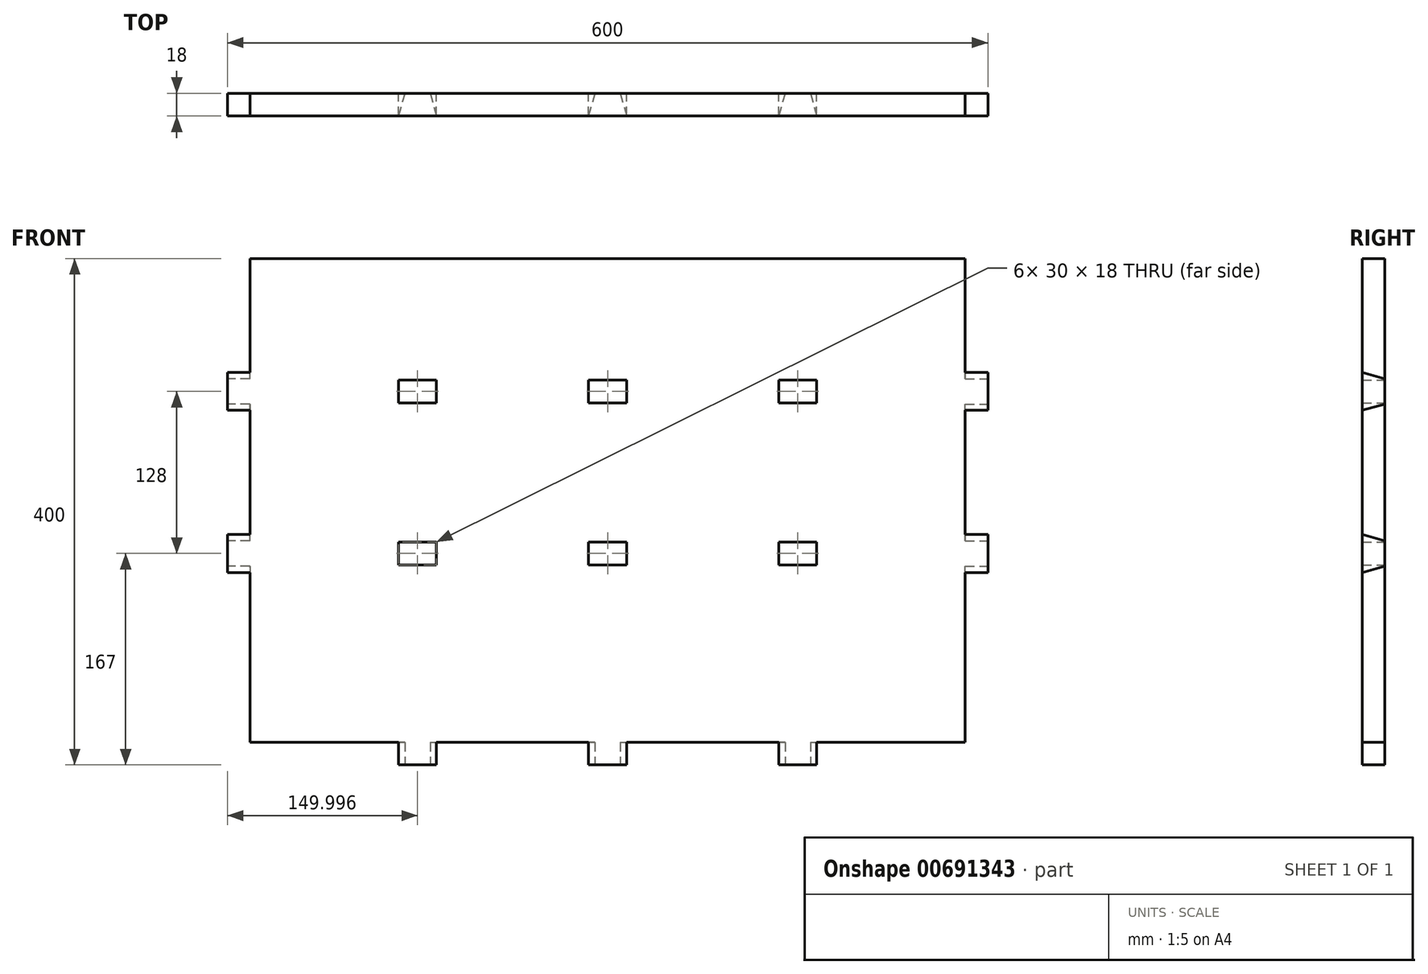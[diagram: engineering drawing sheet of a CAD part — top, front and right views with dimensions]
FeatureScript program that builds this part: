
annotation { "Feature Type Name" : "Feature", "Feature Type Description" : "" }
export const myFeature = defineFeature(function(context is Context, id is Id, definition is map)
    precondition{}
    {
        {
            var Q0;
            Q0=qCreatedBy(makeId("Top.planeOp"),FACE);
            var sketch = newSketch(context, id + "F0", { "sketchPlane" : qUnion([Q0])});
            skLineSegment(sketch, "E0", {"start": v(-0.06, -318.27) * mm, "end": v(-0.06, 208.58) * mm, "construction": true});
            skLineSegment(sketch, "E1", {"start": v(-352.66, -70.99) * mm, "end": v(361, -70.99) * mm, "construction": true});
            skLineSegment(sketch, "E2", {"start": v(-10.06, 129.01) * mm, "end": v(-15.06, 111.01) * mm});
            skLineSegment(sketch, "E3", {"start": v(-15.06, 111.01) * mm, "end": v(-0.06, 111.01) * mm});
            skLineSegment(sketch, "E4", {"start": v(-10.06, 129.01) * mm, "end": v(-0.06, 129.01) * mm});
            skLineSegment(sketch, "E5.MirrorCS", {"start": v(9.94, 129.01) * mm, "end": v(14.94, 111.01) * mm});
            skLineSegment(sketch, "E6", {"start": v(-0.06, 111.01) * mm, "end": v(14.94, 111.01) * mm});
            skLineSegment(sketch, "E7", {"start": v(-0.06, 129.01) * mm, "end": v(9.94, 129.01) * mm});
            skLineSegment(sketch, "E8.1.0.0", {"start": v(139.94, 129.01) * mm, "end": v(134.94, 111.01) * mm});
            skLineSegment(sketch, "E8.1.0.1", {"start": v(139.94, 129.01) * mm, "end": v(149.94, 129.01) * mm});
            skLineSegment(sketch, "E8.1.0.2", {"start": v(149.94, 129.01) * mm, "end": v(159.94, 129.01) * mm});
            skLineSegment(sketch, "E8.1.0.3", {"start": v(159.94, 129.01) * mm, "end": v(164.94, 111.01) * mm});
            skLineSegment(sketch, "E9.1.0.0", {"start": v(-160.06, 129.01) * mm, "end": v(-165.06, 111.01) * mm});
            skLineSegment(sketch, "E9.1.0.1", {"start": v(-160.06, 129.01) * mm, "end": v(-150.06, 129.01) * mm});
            skLineSegment(sketch, "E9.1.0.2", {"start": v(-150.06, 129.01) * mm, "end": v(-140.06, 129.01) * mm});
            skLineSegment(sketch, "E9.1.0.3", {"start": v(-140.06, 129.01) * mm, "end": v(-135.06, 111.01) * mm});
            skLineSegment(sketch, "E10", {"start": v(164.94, 111.01) * mm, "end": v(134.94, 111.01) * mm});
            skLineSegment(sketch, "E11", {"start": v(-135.06, 111.01) * mm, "end": v(-165.06, 111.01) * mm});
            skLineSegment(sketch, "E12", {"start": v(-300.06, -10.99) * mm, "end": v(-300.06, -0.99) * mm, "construction": true});
            skLineSegment(sketch, "E13", {"start": v(-300.06, -0.99) * mm, "end": v(-282.06, -0.99) * mm, "construction": true});
            skLineSegment(sketch, "E14", {"start": v(-300.06, -0.99) * mm, "end": v(-300.06, 9.01) * mm});
            skLineSegment(sketch, "E15", {"start": v(-300.06, 9.01) * mm, "end": v(-282.06, 14.01) * mm});
            skLineSegment(sketch, "E16", {"start": v(-282.06, 14.01) * mm, "end": v(-282.06, -0.99) * mm});
            skLineSegment(sketch, "E17.MirrorCS", {"start": v(-300.06, -0.99) * mm, "end": v(-300.06, -10.99) * mm});
            skLineSegment(sketch, "E18.MirrorCS", {"start": v(-300.06, -10.99) * mm, "end": v(-282.06, -15.99) * mm});
            skLineSegment(sketch, "E19.MirrorCS", {"start": v(-282.06, -15.99) * mm, "end": v(-282.06, -0.99) * mm});
            skLineSegment(sketch, "E20.MirrorCS", {"start": v(-300.06, -130.99) * mm, "end": v(-282.06, -125.99) * mm});
            skLineSegment(sketch, "E21.MirrorCS", {"start": v(-282.06, -125.99) * mm, "end": v(-282.06, -140.99) * mm});
            skLineSegment(sketch, "E22.MirrorCS", {"start": v(-282.06, -155.99) * mm, "end": v(-282.06, -140.99) * mm});
            skLineSegment(sketch, "E23.MirrorCS", {"start": v(-300.06, -150.99) * mm, "end": v(-282.06, -155.99) * mm});
            skLineSegment(sketch, "E24.MirrorCS", {"start": v(-300.06, -140.99) * mm, "end": v(-300.06, -150.99) * mm});
            skLineSegment(sketch, "E25.MirrorCS", {"start": v(299.94, 9.01) * mm, "end": v(281.94, 14.01) * mm});
            skLineSegment(sketch, "E26.MirrorCS", {"start": v(281.94, 14.01) * mm, "end": v(281.94, -0.99) * mm});
            skLineSegment(sketch, "E27.MirrorCS", {"start": v(299.94, -0.99) * mm, "end": v(299.94, 9.01) * mm});
            skLineSegment(sketch, "E28.MirrorCS", {"start": v(299.94, -10.99) * mm, "end": v(281.94, -15.99) * mm});
            skLineSegment(sketch, "E29.MirrorCS", {"start": v(281.94, -15.99) * mm, "end": v(281.94, -0.99) * mm});
            skLineSegment(sketch, "E30.MirrorCS", {"start": v(299.94, -0.99) * mm, "end": v(299.94, -10.99) * mm});
            skLineSegment(sketch, "E31.MirrorCS", {"start": v(299.94, -0.99) * mm, "end": v(281.94, -0.99) * mm, "construction": true});
            skLineSegment(sketch, "E32.MirrorCS", {"start": v(299.94, -150.99) * mm, "end": v(281.94, -155.99) * mm});
            skLineSegment(sketch, "E33.MirrorCS", {"start": v(281.94, -125.99) * mm, "end": v(281.94, -140.99) * mm});
            skLineSegment(sketch, "E34.MirrorCS", {"start": v(281.94, -155.99) * mm, "end": v(281.94, -140.99) * mm});
            skLineSegment(sketch, "E35.MirrorCS", {"start": v(299.94, -130.99) * mm, "end": v(281.94, -125.99) * mm});
            skLineSegment(sketch, "E36.MirrorCS", {"start": v(299.94, -140.99) * mm, "end": v(299.94, -150.99) * mm});
            skLineSegment(sketch, "E37.MirrorCS", {"start": v(299.94, -10.99) * mm, "end": v(299.94, -0.99) * mm, "construction": true});
            skLineSegment(sketch, "E38", {"start": v(-300.06, -140.99) * mm, "end": v(-300.06, -130.99) * mm});
            skLineSegment(sketch, "E39", {"start": v(299.94, -140.99) * mm, "end": v(299.94, -130.99) * mm});
            skPoint(sketch, "E40.orphan", {"position": v(299.94, -70.99) * mm});
            skPoint(sketch, "E41.orphan", {"position": v(-300.06, -70.99) * mm});
            skSolve(sketch);
        }
        {
            var Q0;
            Q0=qCreatedBy(makeId("Front.planeOp"),FACE);
            var Q1;
            Q1=sQuery(id+"F0.wireOp",VERTEX,"E2.start");
            cPlane(context, id + "F1", {"entities" : qUnion([Q0, Q1]), "cplaneType" : CPlaneType.PLANE_POINT, "offset" : 150 * mm, "oppositeDirection" : true, "width" : 150 * mm, "height" : 150 * mm});
        }
        {
            var Q0;
            Q0=qCreatedBy(makeId("Right.planeOp"),FACE);
            var Q1;
            Q1=sQuery(id+"F0.wireOp",VERTEX,"E28.MirrorCS.start");
            cPlane(context, id + "F2", {"entities" : qUnion([Q0, Q1]), "cplaneType" : CPlaneType.PLANE_POINT, "offset" : 25 * mm, "width" : 150 * mm, "height" : 150 * mm});
        }
        {
            var Q0;
            Q0=qCreatedBy(id+"F2.planeOp",FACE);
            var sketch = newSketch(context, id + "F3", { "sketchPlane" : qUnion([Q0])});
            skPoint(sketch, "E42.0", {"position": v(-150.99, 0) * mm});
            skLineSegment(sketch, "E43.0", {"start": v(-150.99, 18) * mm, "end": v(-150.99, 0) * mm});
            skLineSegment(sketch, "E44.0", {"start": v(-150.99, 18) * mm, "end": v(-130.99, 18) * mm});
            skLineSegment(sketch, "E45.0", {"start": v(-130.99, 18) * mm, "end": v(-130.99, 0) * mm});
            skLineSegment(sketch, "E46.0", {"start": v(-150.99, 0) * mm, "end": v(-130.99, 0) * mm});
            skLineSegment(sketch, "E47.0.0", {"start": v(-10.99, 0) * mm, "end": v(9.01, 0) * mm});
            skLineSegment(sketch, "E47.0.1", {"start": v(9.01, 0) * mm, "end": v(9.01, 18) * mm});
            skLineSegment(sketch, "E47.0.2", {"start": v(9.01, 18) * mm, "end": v(-10.99, 18) * mm});
            skLineSegment(sketch, "E47.0.3", {"start": v(-10.99, 18) * mm, "end": v(-10.99, 0) * mm});
            skLineSegment(sketch, "E48.0", {"start": v(-270.99, 0) * mm, "end": v(-150.99, 0) * mm});
            skLineSegment(sketch, "E49.0", {"start": v(-70.99, 0) * mm, "end": v(-130.99, 0) * mm});
            skLineSegment(sketch, "E50.0", {"start": v(-70.99, 0) * mm, "end": v(-10.99, 0) * mm});
            skLineSegment(sketch, "E51.0", {"start": v(129.01, 0) * mm, "end": v(9.01, 0) * mm});
            skLineSegment(sketch, "E52", {"start": v(-130.99, 18) * mm, "end": v(-10.99, 18) * mm});
            skLineSegment(sketch, "E53", {"start": v(-150.99, 18) * mm, "end": v(-270.99, 18) * mm});
            skLineSegment(sketch, "E54", {"start": v(9.01, 18) * mm, "end": v(129.01, 18) * mm});
            skLineSegment(sketch, "E55", {"start": v(-270.99, 18) * mm, "end": v(-270.99, 0) * mm});
            skLineSegment(sketch, "E56", {"start": v(129.01, 18) * mm, "end": v(129.01, 0) * mm});
            skLineSegment(sketch, "E57.bottom", {"start": v(129.01, 18) * mm, "end": v(-270.99, 18) * mm});
            skLineSegment(sketch, "E57.top", {"start": v(129.01, 400) * mm, "end": v(-270.99, 400) * mm});
            skLineSegment(sketch, "E57.left", {"start": v(129.01, 18) * mm, "end": v(129.01, 400) * mm});
            skLineSegment(sketch, "E57.right", {"start": v(-270.99, 18) * mm, "end": v(-270.99, 400) * mm});
            skLineSegment(sketch, "E58", {"start": v(-140.99, 18) * mm, "end": v(-140.99, 313.42) * mm, "construction": true});
            skLineSegment(sketch, "E59", {"start": v(-0.99, 18) * mm, "end": v(-0.99, 349.98) * mm, "construction": true});
            skLineSegment(sketch, "E60", {"start": v(-312.14, 158) * mm, "end": v(190.47, 158) * mm, "construction": true});
            skLineSegment(sketch, "E61", {"start": v(-304.14, 286) * mm, "end": v(174.47, 286) * mm, "construction": true});
            skLineSegment(sketch, "E62", {"start": v(-312.14, 176) * mm, "end": v(194.1, 176) * mm, "construction": true});
            skLineSegment(sketch, "E63", {"start": v(-306.06, 304) * mm, "end": v(175.74, 304) * mm, "construction": true});
            skLineSegment(sketch, "E64", {"start": v(173.45, 391) * mm, "end": v(-324.33, 391) * mm, "construction": true});
            skLineSegment(sketch, "E65.bottom", {"start": v(-140.99, 176) * mm, "end": v(-125.99, 176) * mm});
            skLineSegment(sketch, "E65.top", {"start": v(-140.99, 158) * mm, "end": v(-125.99, 158) * mm});
            skLineSegment(sketch, "E65.left", {"start": v(-140.99, 176) * mm, "end": v(-140.99, 158) * mm});
            skLineSegment(sketch, "E65.right", {"start": v(-125.99, 176) * mm, "end": v(-125.99, 158) * mm});
            skLineSegment(sketch, "E66.MirrorCS", {"start": v(-155.99, 176) * mm, "end": v(-155.99, 158) * mm});
            skLineSegment(sketch, "E67", {"start": v(-140.99, 158) * mm, "end": v(-155.99, 158) * mm});
            skLineSegment(sketch, "E68", {"start": v(-155.99, 176) * mm, "end": v(-140.99, 176) * mm});
            skLineSegment(sketch, "E69.1.0.0", {"start": v(14.01, 176) * mm, "end": v(14.01, 158) * mm});
            skLineSegment(sketch, "E69.1.0.1", {"start": v(-15.99, 176) * mm, "end": v(-15.99, 158) * mm});
            skLineSegment(sketch, "E69.direction1", {"start": v(-125.99, 158) * mm, "end": v(14.01, 158) * mm, "construction": true});
            skLineSegment(sketch, "E70", {"start": v(-15.99, 176) * mm, "end": v(14.01, 176) * mm});
            skLineSegment(sketch, "E71", {"start": v(-15.99, 158) * mm, "end": v(14.01, 158) * mm});
            skLineSegment(sketch, "E72", {"start": v(-155.99, 176) * mm, "end": v(-155.99, 421.76) * mm, "construction": true});
            skLineSegment(sketch, "E73", {"start": v(-125.99, 176) * mm, "end": v(-125.99, 428.96) * mm, "construction": true});
            skLineSegment(sketch, "E74", {"start": v(-15.99, 176) * mm, "end": v(-15.99, 432.16) * mm, "construction": true});
            skLineSegment(sketch, "E75", {"start": v(14.01, 176) * mm, "end": v(14.01, 435.36) * mm, "construction": true});
            skLineSegment(sketch, "E76.bottom", {"start": v(-155.99, 304) * mm, "end": v(-125.99, 304) * mm});
            skLineSegment(sketch, "E76.top", {"start": v(-155.99, 286) * mm, "end": v(-125.99, 286) * mm});
            skLineSegment(sketch, "E76.left", {"start": v(-155.99, 304) * mm, "end": v(-155.99, 286) * mm});
            skLineSegment(sketch, "E76.right", {"start": v(-125.99, 304) * mm, "end": v(-125.99, 286) * mm});
            skLineSegment(sketch, "E77.bottom", {"start": v(14.01, 286) * mm, "end": v(-15.99, 286) * mm});
            skLineSegment(sketch, "E77.top", {"start": v(14.01, 304) * mm, "end": v(-15.99, 304) * mm});
            skLineSegment(sketch, "E77.left", {"start": v(14.01, 286) * mm, "end": v(14.01, 304) * mm});
            skLineSegment(sketch, "E77.right", {"start": v(-15.99, 286) * mm, "end": v(-15.99, 304) * mm});
            skLineSegment(sketch, "E78", {"start": v(111.01, 481.52) * mm, "end": v(111.01, -48.3) * mm, "construction": true});
            skLineSegment(sketch, "E79", {"start": v(14.01, 167) * mm, "end": v(206.7, 167) * mm, "construction": true});
            skLineSegment(sketch, "E80", {"start": v(14.01, 295) * mm, "end": v(175.74, 295) * mm, "construction": true});
            skLineSegment(sketch, "E81", {"start": v(111.01, 295) * mm, "end": v(111.01, 310) * mm});
            skLineSegment(sketch, "E82", {"start": v(111.01, 310) * mm, "end": v(129.01, 305) * mm});
            skLineSegment(sketch, "E83", {"start": v(129.01, 305) * mm, "end": v(129.01, 295) * mm});
            skLineSegment(sketch, "E84.MirrorCS", {"start": v(111.01, 280) * mm, "end": v(129.01, 285) * mm});
            skLineSegment(sketch, "E85", {"start": v(111.01, 295) * mm, "end": v(111.01, 280) * mm});
            skLineSegment(sketch, "E86", {"start": v(129.01, 285) * mm, "end": v(129.01, 295) * mm, "construction": true});
            skLineSegment(sketch, "E87.0.1.0", {"start": v(111.01, 152) * mm, "end": v(129.01, 157) * mm});
            skLineSegment(sketch, "E87.0.1.1", {"start": v(111.01, 182) * mm, "end": v(129.01, 177) * mm});
            skLineSegment(sketch, "E87.direction1", {"start": v(111.01, 280) * mm, "end": v(136.01, 280) * mm, "construction": true});
            skLineSegment(sketch, "E87.direction2", {"start": v(111.01, 280) * mm, "end": v(111.01, 152) * mm, "construction": true});
            skLineSegment(sketch, "E88", {"start": v(111.01, 182) * mm, "end": v(111.01, 152) * mm});
            skLineSegment(sketch, "E89", {"start": v(129.01, 157) * mm, "end": v(129.01, 177) * mm});
            skLineSegment(sketch, "E90", {"start": v(129.01, 305) * mm, "end": v(129.01, 285) * mm});
            skLineSegment(sketch, "E91", {"start": v(111.01, 280) * mm, "end": v(111.01, 310) * mm});
            skSolve(sketch);
        }
        {
            var Q0;
            Q0=qCreatedBy(id+"F1.planeOp",FACE);
            var sketch = newSketch(context, id + "F4", { "sketchPlane" : qUnion([Q0])});
            skLineSegment(sketch, "E92.bottom", {"start": v(-300.2, 0) * mm, "end": v(299.94, 0) * mm});
            skLineSegment(sketch, "E92.top", {"start": v(-300.2, 400) * mm, "end": v(299.94, 400) * mm});
            skLineSegment(sketch, "E92.left", {"start": v(-300.2, 0) * mm, "end": v(-300.2, 400) * mm});
            skLineSegment(sketch, "E92.right", {"start": v(299.94, 0) * mm, "end": v(299.94, 400) * mm});
            skLineSegment(sketch, "E93.0", {"start": v(281.94, 0) * mm, "end": v(281.94, 400) * mm});
            skLineSegment(sketch, "E94.0", {"start": v(-282.2, 0) * mm, "end": v(-282.2, 400) * mm});
            skLineSegment(sketch, "E95.0", {"start": v(-300.2, 18) * mm, "end": v(299.94, 18) * mm});
            skSolve(sketch);
        }
        {
            var Q0;
            {var subQ0=sQuery(id+"F4.wireOp",EDGE,"E93.0");var subQ1=sQuery(id+"F4.wireOp",EDGE,"E92.top");var subQ2=makeQuery(id+"F4.imprint","INTERSECT",VERTEX,{"derivedFrom":[subQ1,subQ0]});Q0=makeQuery(id+"F4.imprint","IMPRINT",FACE,{"disambiguationData":[TD([[makeQuery(id+"F4.imprint","IMPRINT",EDGE,{"disambiguationData":[TD([[subQ2,1.0]])],"derivedFrom":subQ1}),-1.0]])]});}
            extrude(context, id + "F5", {"entities" : qUnion([Q0]), "depth" : 18 * mm, "offsetDistance" : 25 * mm});
        }
        {
            var Q0;
            Q0=makeQuery(id+"F0.imprint","IMPRINT",FACE,{"disambiguationData":[TD([[makeQuery(id+"F0.imprint","IMPRINT",EDGE,{"derivedFrom":sQuery(id+"F0.wireOp",EDGE,"E8.1.0.0")}),1.0]])]});
            var Q1;
            Q1=makeQuery(id+"F0.imprint","IMPRINT",FACE,{"disambiguationData":[TD([[makeQuery(id+"F0.imprint","IMPRINT",EDGE,{"derivedFrom":sQuery(id+"F0.wireOp",EDGE,"E2")}),1.0]])]});
            var Q2;
            Q2=makeQuery(id+"F0.imprint","IMPRINT",FACE,{"disambiguationData":[TD([[makeQuery(id+"F0.imprint","IMPRINT",EDGE,{"derivedFrom":sQuery(id+"F0.wireOp",EDGE,"E9.1.0.0")}),1.0]])]});
            var Q3;
            Q3=makeQuery(id+"F5.opExtrude","SWEPT_FACE",FACE,{"disambiguationData":[OSD([sQuery(id+"F4.wireOp",EDGE,"E95.0")])]});
            extrude(context, id + "F6", {"entities" : qUnion([Q0, Q1, Q2]), "operationType" : NewBodyOperationType.ADD, "endBound" : BoundingType.UP_TO_SURFACE, "depth" : 18 * mm, "endBoundEntityFace" : qUnion([Q3]), "offsetDistance" : 25 * mm});
        }
        {
            var Q0;
            Q0=makeQuery(id+"F3.imprint","IMPRINT",FACE,{"disambiguationData":[TD([[makeQuery(id+"F3.imprint","IMPRINT",EDGE,{"derivedFrom":sQuery(id+"F3.wireOp",EDGE,"E87.0.1.0")}),1.0]])]});
            var Q1;
            {var subQ0=sQuery(id+"F3.wireOp",EDGE,"E82");Q1=makeQuery(id+"F3.imprint","IMPRINT",FACE,{"disambiguationData":[TD([[makeQuery(id+"F3.imprint","IMPRINT",EDGE,{"derivedFrom":subQ0}),-1.0]])]});}
            var Q2;
            Q2=makeQuery(id+"F5.opExtrude","SWEPT_FACE",FACE,{"disambiguationData":[OSD([sQuery(id+"F4.wireOp",EDGE,"E93.0")])]});
            extrude(context, id + "F7", {"entities" : qUnion([Q0, Q1]), "operationType" : NewBodyOperationType.ADD, "endBound" : BoundingType.UP_TO_SURFACE, "oppositeDirection" : true, "depth" : 25 * mm, "endBoundEntityFace" : qUnion([Q2]), "offsetDistance" : 25 * mm});
        }
        {
            var Q0;
            Q0=qCreatedBy(id+"F2.planeOp",FACE);
            cPlane(context, id + "F8", {"entities" : qUnion([Q0]), "cplaneType" : CPlaneType.OFFSET, "offset" : 600 * mm, "oppositeDirection" : true, "width" : 150 * mm, "height" : 150 * mm});
        }
        {
            var Q0;
            Q0=qCreatedBy(id+"F8.planeOp",FACE);
            var sketch = newSketch(context, id + "F9", { "sketchPlane" : qUnion([Q0])});
            skPoint(sketch, "E96.0", {"position": v(-150.99, 0) * mm});
            skLineSegment(sketch, "E97.0", {"start": v(-150.99, 18) * mm, "end": v(-150.99, 0) * mm});
            skLineSegment(sketch, "E98.0", {"start": v(-150.99, 18) * mm, "end": v(-130.99, 18) * mm});
            skLineSegment(sketch, "E99.0", {"start": v(-130.99, 18) * mm, "end": v(-130.99, 0) * mm});
            skLineSegment(sketch, "E100.0", {"start": v(-150.99, 0) * mm, "end": v(-130.99, 0) * mm});
            skLineSegment(sketch, "E101.0.0", {"start": v(-10.99, 0) * mm, "end": v(9.01, 0) * mm});
            skLineSegment(sketch, "E101.0.1", {"start": v(9.01, 0) * mm, "end": v(9.01, 18) * mm});
            skLineSegment(sketch, "E101.0.2", {"start": v(9.01, 18) * mm, "end": v(-10.99, 18) * mm});
            skLineSegment(sketch, "E101.0.3", {"start": v(-10.99, 18) * mm, "end": v(-10.99, 0) * mm});
            skLineSegment(sketch, "E102.0", {"start": v(-270.99, 0) * mm, "end": v(-150.99, 0) * mm});
            skLineSegment(sketch, "E103.0", {"start": v(-70.99, 0) * mm, "end": v(-130.99, 0) * mm});
            skLineSegment(sketch, "E104.0", {"start": v(-70.99, 0) * mm, "end": v(-10.99, 0) * mm});
            skLineSegment(sketch, "E105.0", {"start": v(129.01, 0) * mm, "end": v(9.01, 0) * mm});
            skLineSegment(sketch, "E106", {"start": v(-130.99, 18) * mm, "end": v(-10.99, 18) * mm});
            skLineSegment(sketch, "E107", {"start": v(-150.99, 18) * mm, "end": v(-270.99, 18) * mm});
            skLineSegment(sketch, "E108", {"start": v(9.01, 18) * mm, "end": v(129.01, 18) * mm});
            skLineSegment(sketch, "E109", {"start": v(-270.99, 18) * mm, "end": v(-270.99, 0) * mm});
            skLineSegment(sketch, "E110", {"start": v(129.01, 18) * mm, "end": v(129.01, 0) * mm});
            skLineSegment(sketch, "E111.bottom", {"start": v(129.01, 18) * mm, "end": v(-270.99, 18) * mm});
            skLineSegment(sketch, "E111.top", {"start": v(129.01, 400) * mm, "end": v(-270.99, 400) * mm});
            skLineSegment(sketch, "E111.left", {"start": v(129.01, 18) * mm, "end": v(129.01, 400) * mm});
            skLineSegment(sketch, "E111.right", {"start": v(-270.99, 18) * mm, "end": v(-270.99, 400) * mm});
            skLineSegment(sketch, "E112", {"start": v(-140.99, 18) * mm, "end": v(-140.99, 313.42) * mm, "construction": true});
            skLineSegment(sketch, "E113", {"start": v(-0.99, 18) * mm, "end": v(-0.99, 349.98) * mm, "construction": true});
            skLineSegment(sketch, "E114", {"start": v(-312.14, 158) * mm, "end": v(190.47, 158) * mm, "construction": true});
            skLineSegment(sketch, "E115", {"start": v(-304.14, 286) * mm, "end": v(174.47, 286) * mm, "construction": true});
            skLineSegment(sketch, "E116", {"start": v(-312.14, 176) * mm, "end": v(194.1, 176) * mm, "construction": true});
            skLineSegment(sketch, "E117", {"start": v(-306.06, 304) * mm, "end": v(175.74, 304) * mm, "construction": true});
            skLineSegment(sketch, "E118", {"start": v(173.45, 391) * mm, "end": v(-324.33, 391) * mm, "construction": true});
            skLineSegment(sketch, "E119.bottom", {"start": v(-140.99, 176) * mm, "end": v(-125.99, 176) * mm});
            skLineSegment(sketch, "E119.top", {"start": v(-140.99, 158) * mm, "end": v(-125.99, 158) * mm});
            skLineSegment(sketch, "E119.left", {"start": v(-140.99, 176) * mm, "end": v(-140.99, 158) * mm});
            skLineSegment(sketch, "E119.right", {"start": v(-125.99, 176) * mm, "end": v(-125.99, 158) * mm});
            skLineSegment(sketch, "E120.MirrorCS", {"start": v(-155.99, 176) * mm, "end": v(-155.99, 158) * mm});
            skLineSegment(sketch, "E121", {"start": v(-140.99, 158) * mm, "end": v(-155.99, 158) * mm});
            skLineSegment(sketch, "E122", {"start": v(-155.99, 176) * mm, "end": v(-140.99, 176) * mm});
            skLineSegment(sketch, "E123.1.0.0", {"start": v(14.01, 176) * mm, "end": v(14.01, 158) * mm});
            skLineSegment(sketch, "E123.1.0.1", {"start": v(-15.99, 176) * mm, "end": v(-15.99, 158) * mm});
            skLineSegment(sketch, "E123.direction1", {"start": v(-125.99, 158) * mm, "end": v(14.01, 158) * mm, "construction": true});
            skLineSegment(sketch, "E124", {"start": v(-15.99, 176) * mm, "end": v(14.01, 176) * mm});
            skLineSegment(sketch, "E125", {"start": v(-15.99, 158) * mm, "end": v(14.01, 158) * mm});
            skLineSegment(sketch, "E126", {"start": v(-155.99, 176) * mm, "end": v(-155.99, 421.76) * mm, "construction": true});
            skLineSegment(sketch, "E127", {"start": v(-125.99, 176) * mm, "end": v(-125.99, 428.96) * mm, "construction": true});
            skLineSegment(sketch, "E128", {"start": v(-15.99, 176) * mm, "end": v(-15.99, 432.16) * mm, "construction": true});
            skLineSegment(sketch, "E129", {"start": v(14.01, 176) * mm, "end": v(14.01, 435.36) * mm, "construction": true});
            skLineSegment(sketch, "E130.bottom", {"start": v(-155.99, 304) * mm, "end": v(-125.99, 304) * mm});
            skLineSegment(sketch, "E130.top", {"start": v(-155.99, 286) * mm, "end": v(-125.99, 286) * mm});
            skLineSegment(sketch, "E130.left", {"start": v(-155.99, 304) * mm, "end": v(-155.99, 286) * mm});
            skLineSegment(sketch, "E130.right", {"start": v(-125.99, 304) * mm, "end": v(-125.99, 286) * mm});
            skLineSegment(sketch, "E131.bottom", {"start": v(14.01, 286) * mm, "end": v(-15.99, 286) * mm});
            skLineSegment(sketch, "E131.top", {"start": v(14.01, 304) * mm, "end": v(-15.99, 304) * mm});
            skLineSegment(sketch, "E131.left", {"start": v(14.01, 286) * mm, "end": v(14.01, 304) * mm});
            skLineSegment(sketch, "E131.right", {"start": v(-15.99, 286) * mm, "end": v(-15.99, 304) * mm});
            skLineSegment(sketch, "E132", {"start": v(111.01, 481.52) * mm, "end": v(111.01, -48.3) * mm, "construction": true});
            skLineSegment(sketch, "E133", {"start": v(14.01, 167) * mm, "end": v(206.7, 167) * mm, "construction": true});
            skLineSegment(sketch, "E134", {"start": v(14.01, 295) * mm, "end": v(175.74, 295) * mm, "construction": true});
            skLineSegment(sketch, "E135", {"start": v(111.01, 295) * mm, "end": v(111.01, 310) * mm});
            skLineSegment(sketch, "E136", {"start": v(111.01, 310) * mm, "end": v(129.01, 305) * mm});
            skLineSegment(sketch, "E137", {"start": v(129.01, 305) * mm, "end": v(129.01, 295) * mm});
            skLineSegment(sketch, "E138.MirrorCS", {"start": v(111.01, 280) * mm, "end": v(129.01, 285) * mm});
            skLineSegment(sketch, "E139", {"start": v(111.01, 295) * mm, "end": v(111.01, 280) * mm});
            skLineSegment(sketch, "E140", {"start": v(129.01, 285) * mm, "end": v(129.01, 295) * mm, "construction": true});
            skLineSegment(sketch, "E141.0.1.0", {"start": v(111.01, 152) * mm, "end": v(129.01, 157) * mm});
            skLineSegment(sketch, "E141.0.1.1", {"start": v(111.01, 182) * mm, "end": v(129.01, 177) * mm});
            skLineSegment(sketch, "E141.direction1", {"start": v(111.01, 280) * mm, "end": v(136.01, 280) * mm, "construction": true});
            skLineSegment(sketch, "E141.direction2", {"start": v(111.01, 280) * mm, "end": v(111.01, 152) * mm, "construction": true});
            skLineSegment(sketch, "E142", {"start": v(111.01, 182) * mm, "end": v(111.01, 152) * mm});
            skLineSegment(sketch, "E143", {"start": v(129.01, 157) * mm, "end": v(129.01, 177) * mm});
            skLineSegment(sketch, "E144", {"start": v(129.01, 305) * mm, "end": v(129.01, 285) * mm});
            skLineSegment(sketch, "E145", {"start": v(111.01, 280) * mm, "end": v(111.01, 310) * mm});
            skSolve(sketch);
        }
        {
            var Q0;
            {var subQ0=sQuery(id+"F9.wireOp",EDGE,"E136");Q0=makeQuery(id+"F9.imprint","IMPRINT",FACE,{"disambiguationData":[TD([[makeQuery(id+"F9.imprint","IMPRINT",EDGE,{"derivedFrom":subQ0}),-1.0]])]});}
            var Q1;
            Q1=makeQuery(id+"F9.imprint","IMPRINT",FACE,{"disambiguationData":[TD([[makeQuery(id+"F9.imprint","IMPRINT",EDGE,{"derivedFrom":sQuery(id+"F9.wireOp",EDGE,"E141.0.1.0")}),1.0]])]});
            var Q2;
            Q2=makeQuery(id+"F5.opExtrude","SWEPT_FACE",FACE,{"disambiguationData":[OSD([sQuery(id+"F4.wireOp",EDGE,"E94.0")])]});
            extrude(context, id + "F10", {"entities" : qUnion([Q0, Q1]), "operationType" : NewBodyOperationType.ADD, "endBound" : BoundingType.UP_TO_SURFACE, "depth" : 25 * mm, "endBoundEntityFace" : qUnion([Q2]), "offsetDistance" : 25 * mm});
        }
        {
            var Q0;
            Q0=qCreatedBy(id+"F1.planeOp",FACE);
            var sketch = newSketch(context, id + "F11", { "sketchPlane" : qUnion([Q0])});
            skLineSegment(sketch, "E146", {"start": v(317.76, 295) * mm, "end": v(164.94, 295) * mm});
            skLineSegment(sketch, "E147", {"start": v(321.01, 167) * mm, "end": v(164.94, 167) * mm});
            skLineSegment(sketch, "E148", {"start": v(149.94, -9.4) * mm, "end": v(149.94, 158) * mm});
            skLineSegment(sketch, "E149", {"start": v(-0.06, -7.65) * mm, "end": v(-0.06, 441.55) * mm, "construction": true});
            skLineSegment(sketch, "E150", {"start": v(-150.06, -10.32) * mm, "end": v(-150.06, 286) * mm, "construction": true});
            skLineSegment(sketch, "E151.0", {"start": v(321.01, 176) * mm, "end": v(-308.2, 176) * mm});
            skLineSegment(sketch, "E152.0", {"start": v(321.01, 158) * mm, "end": v(-308.2, 158) * mm});
            skLineSegment(sketch, "E153.0", {"start": v(317.76, 304) * mm, "end": v(-314.39, 304) * mm});
            skLineSegment(sketch, "E154.0", {"start": v(317.76, 286) * mm, "end": v(-314.39, 286) * mm});
            skLineSegment(sketch, "E155.0", {"start": v(164.94, -9.4) * mm, "end": v(164.94, 429.65) * mm});
            skLineSegment(sketch, "E156.0", {"start": v(134.94, -9.4) * mm, "end": v(134.94, 429.65) * mm});
            skLineSegment(sketch, "E157.0", {"start": v(14.94, -7.65) * mm, "end": v(14.94, 441.55) * mm});
            skLineSegment(sketch, "E158.0", {"start": v(-15.06, -7.65) * mm, "end": v(-15.06, 441.55) * mm});
            skLineSegment(sketch, "E159.0", {"start": v(-135.06, -10.32) * mm, "end": v(-135.06, 434.8) * mm});
            skLineSegment(sketch, "E160.0", {"start": v(-165.06, -10.32) * mm, "end": v(-165.06, 434.8) * mm});
            skLineSegment(sketch, "E161.trimOffspring", {"start": v(149.94, 304) * mm, "end": v(149.94, 429.65) * mm});
            skLineSegment(sketch, "E162.trimOffspring", {"start": v(134.94, 295) * mm, "end": v(14.94, 295) * mm});
            skLineSegment(sketch, "E163.trimOffspring", {"start": v(-15.06, 295) * mm, "end": v(-135.06, 295) * mm});
            skLineSegment(sketch, "E164.trimOffspring", {"start": v(134.94, 167) * mm, "end": v(14.94, 167) * mm});
            skLineSegment(sketch, "E165.trimOffspring", {"start": v(149.94, 176) * mm, "end": v(149.94, 286) * mm});
            skLineSegment(sketch, "E166.trimOffspring", {"start": v(-15.06, 167) * mm, "end": v(-135.06, 167) * mm});
            skLineSegment(sketch, "E167.trimOffspring", {"start": v(-165.06, 167) * mm, "end": v(-308.2, 167) * mm});
            skLineSegment(sketch, "E168.trimOffspring", {"start": v(-165.06, 295) * mm, "end": v(-314.39, 295) * mm});
            skLineSegment(sketch, "E169.trimOffspring", {"start": v(-150.06, 304) * mm, "end": v(-150.06, 434.8) * mm, "construction": true});
            skSolve(sketch);
        }
        {
            var Q0;
            {var subQ0=sQuery(id+"F11.wireOp",EDGE,"E152.0");var subQ1=makeQuery(id+"F11.imprint","IMPRINT",VERTEX,{"derivedFrom":subQ0});Q0=makeQuery(id+"F11.imprint","IMPRINT",FACE,{"disambiguationData":[TD([[makeQuery(id+"F11.imprint","IMPRINT",EDGE,{"disambiguationData":[TD([[subQ1,1.0]])],"derivedFrom":subQ0}),-1.0]])]});}
            var Q1;
            {var subQ6=sQuery(id+"F11.wireOp",EDGE,"E153.0");var subQ7=makeQuery(id+"F11.imprint","IMPRINT",VERTEX,{"derivedFrom":subQ6});Q1=makeQuery(id+"F11.imprint","IMPRINT",FACE,{"disambiguationData":[TD([[makeQuery(id+"F11.imprint","IMPRINT",EDGE,{"disambiguationData":[TD([[subQ7,1.0]])],"derivedFrom":subQ6}),1.0]])]});}
            var Q2;
            {var subQ0=sQuery(id+"F11.wireOp",EDGE,"E157.0");var subQ2=sQuery(id+"F11.wireOp",EDGE,"E153.0");var subQ3=makeQuery(id+"F11.imprint","INTERSECT",VERTEX,{"derivedFrom":[subQ2,subQ0]});Q2=makeQuery(id+"F11.imprint","IMPRINT",FACE,{"disambiguationData":[TD([[makeQuery(id+"F11.imprint","IMPRINT",EDGE,{"disambiguationData":[TD([[subQ3,-1.0]])],"derivedFrom":subQ2}),1.0]])]});}
            var Q3;
            {var subQ0=sQuery(id+"F11.wireOp",EDGE,"E157.0");var subQ2=sQuery(id+"F11.wireOp",EDGE,"E151.0");var subQ3=makeQuery(id+"F11.imprint","INTERSECT",VERTEX,{"derivedFrom":[subQ2,subQ0]});Q3=makeQuery(id+"F11.imprint","IMPRINT",FACE,{"disambiguationData":[TD([[makeQuery(id+"F11.imprint","IMPRINT",EDGE,{"disambiguationData":[TD([[subQ3,-1.0]])],"derivedFrom":subQ2}),1.0]])]});}
            var Q4;
            {var subQ4=sQuery(id+"F11.wireOp",EDGE,"E160.0");var subQ9=makeQuery(id+"F11.imprint","IMPRINT",VERTEX,{"disambiguationData":[OD(0.0)],"derivedFrom":subQ4});Q4=makeQuery(id+"F11.imprint","IMPRINT",FACE,{"disambiguationData":[TD([[makeQuery(id+"F11.imprint","IMPRINT",EDGE,{"disambiguationData":[TD([[subQ9,1.0]])],"derivedFrom":subQ4}),-1.0]])]});}
            var Q5;
            {var subQ4=sQuery(id+"F11.wireOp",EDGE,"E160.0");var subQ9=makeQuery(id+"F11.imprint","IMPRINT",VERTEX,{"disambiguationData":[OD(1.0)],"derivedFrom":subQ4});Q5=makeQuery(id+"F11.imprint","IMPRINT",FACE,{"disambiguationData":[TD([[makeQuery(id+"F11.imprint","IMPRINT",EDGE,{"disambiguationData":[TD([[subQ9,1.0]])],"derivedFrom":subQ4}),-1.0]])]});}
            extrude(context, id + "F12", {"entities" : qUnion([Q0, Q1, Q2, Q3, Q4, Q5]), "operationType" : NewBodyOperationType.REMOVE, "depth" : 25 * mm, "offsetDistance" : 25 * mm});
        }
    });
